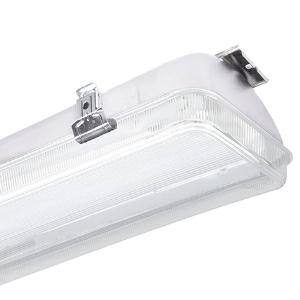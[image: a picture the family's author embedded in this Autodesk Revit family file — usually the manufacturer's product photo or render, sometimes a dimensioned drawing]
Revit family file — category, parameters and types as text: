
# Revit family: 3f_filippi_-_beta_235_75_pc_ampio_3f_filippi_-_52930_-_beta_235_led_752x20_ampio_l655
name_source: partatom
category: Lighting Fixtures
units: mm (PartAtom-declared; Revit-internal decimal feet)

## family parameters
Cut with Voids When Loaded = No
Host = Face
Light Source = No
Part Type = Normal
Room Calculation Point = No
Round Connector Dimension = Use Diameter
Shared = No

## types (1)
- 3F Filippi - Beta 235 75 PC Ampio (1 x LED, 6533 lm, 42 W, 4000 K)
    Apparent Load = 42 VA
    Approval mark = CE
    CIE Flux Codes = 59 89 98 98 100
    Color Rendering = 80
    Color Temperature = 4000 K
    Control Gear = Electronic ballast
    Default Elevation = 1800 mm
    Description = ILLUMINOTECHNICAL
Luminous efficiency 100% (DLOR 99%, ULOR 1%).
Initial luminous flux of the luminaire 6533 lm.
Wide symmetric distribution.
Installation Interdistance Transv.D = 1.40 x hu - Long.D = 1.43 x hu.
Tabular UGR (CIE 117 - 4H-8H; S=0.25H; 70/50/20): RUG 20.8 - 21.2.
Beam angle: 98° - 100°.
Luminous efficacy 156 lm/W.
Lifetime (L93/B10): 30000 h. (tq+25°C)
Lifetime (L90/B10): 50000 h. (tq+25°C)
Lifetime (L85/B10): 80000 h. (tq+25°C)
Lifetime (L80/B10): 100000 h. (tq+25°C)
Lifetime (L85/B10): 50000 h. (tq+45°C)
Sudden decreased luminous flux after 50000 hours: 0% (C0).
Photobiological safety in compliance with IEC/TR 62778: RG0 risk exempt, (IEC 62471).
In compliance with IEC/EN 62722-2-1 - IEC/EN 62717 standards.

SOURCE
2 linear LED modules 20W/840.
Energy efficiency class (UE 2019/2020 - UE 2019/2015): C.
CIE 13.3 Colour rendering index: CRI >80 (R9 <50%).
IES TM-30 Fidelity Index: Rf = 84 Rg = 95.
CCT nominal colour temperature 4000 K.
Colour initial tolerance (MacAdam): SDCM 3.

MECHANICAL
Single-piece housing in pressed steel, powder-coated in white epoxy-polyester.
Polycarbonate screen etched internally, V2 self-extinguishing, UV stabilised, injection moulded.
Ecologic anti-aging injected sealing gasket.
Oversized gear-tray reflector unit in highly reflective white painted hot-galvanised steel.
Methacrylate (PMMA) lenses with external flat surface.
Galvanised steel safety snap-lock clips for diffuser mounting.
Luminaire with limited surface temperature. - D - (EN 60598-2-24)
Dimensions: 655x235 mm, height 140 mm. Weight 4.215 kg.
IP65 protection degree.
Mechanical strength to impacts IK10 (20 joule).
Glow-wire test resistance 850°C.

ELECTRICAL
Halogen Free electronic wiring 230V-50/60Hz, power factor 0.95, THD <25%, constant output current, class I, 1 driver.
Power of the luminaire 42 W.
ENEC - CE.
Flicker: <4%.
Luminaire compliant with EN 60598-2-22 for power supply from a centralised emergency system CPSS (Central Power Supply System), not incorporated in the luminaire - high risk areas excluded. The default power and flux are 100% in AC and 100% in DC.
Ambient temperature from -20°C to +45°C.
Temperature class T6 max 85°C.
Quick connection via M20 3P connector with 9-13 mm tightening range.
Relative humidity UR: <85%.

INSTALLATION
Ceiling / Suspended / Wall.
All accessories dedicated to this product are available on the Catalog and on our website www.3F-Filippi.com.

APPLICATIONS
Suitable product for food production plants (HACCP), IFS (Food Version 6), BRC (GSFS Food Version 7).
Dry, dusty indoor environments, subject to occasional water splashes.
Industrial environments, warehouses, environments where security locks are required on all clips, e.g. prisons.
Environments in which it is necessary a total protection against falling fragments (eg environments with foodstuffs or machines with moving parts or with extreme temperature changes), use luminaires with laminated glass.
Tempered glass is not immune to falling fragments from harmless and caused by shocks or exceptionally derived from the tempering process.

WARNING
Fixture not suitable for cold stores with an ambient temperature <0°C and/or relative humidity >85%.
Luminaire designed for disposal/recycling at end-of-life.
Replaceable (LED only) light source by a professional. Replaceable control gear by a professional.
    Height = 140 mm  [stored 0.459318 ft]
    Lamp = 1 x LED
    Lamp Light Flux = 6533 lm
    Lamp Power = 42 W
    Lamp count = 1
    Length = 655 mm
    Lifetime = 50000 h
    Luminous efficacy = 156 lm/W
    Manufacturer = 3F Filippi
    ModVariant = No
    Model = 3F Filippi - 52930 - Beta 235 LED 752x20 AMPIO L655
    Mounting Place = Ceiling
    Mounting Type = Pendant
    Number of Poles = 1
    OnlyDefault = Yes
    Power Factor = 1
    Product Name = 3F Filippi - Beta 235 75 PC Ampio
    Product group = pendant luminaire
    ProductGroupID = 9
    Protection Class = Protection class I
    Protection Degree = IP 65
    RLX_Detail_Level = 1
    RLX_Emergency_Light_Flux = 0 lm
    RLX_Emergency_Type = 0
    RLX_Emergency_Type_DB = No
    RlxData = <blob elided: 87433 chars, md5=822b9b02>
    Socket = socket
    Standby Power = 0 W
    System Light Flux = 6533 lm
    System Power = 42 W
    Type Comments = Product without accessories
    Type Image = 3ffilippi_52930.jpg
    URL = http://relux.com
    VarID = ---
    Voltage = 0 V
    Weight = 0.00 kg
    Width = 235 mm

note: [stored X ft] marks values corroborated as IEEE doubles in the binary element streams (Revit-internal decimal feet)

## geometry (parser evidence)
native form markers: Blend x4, Sweep x11
no freeform markers — native parametric forms only
